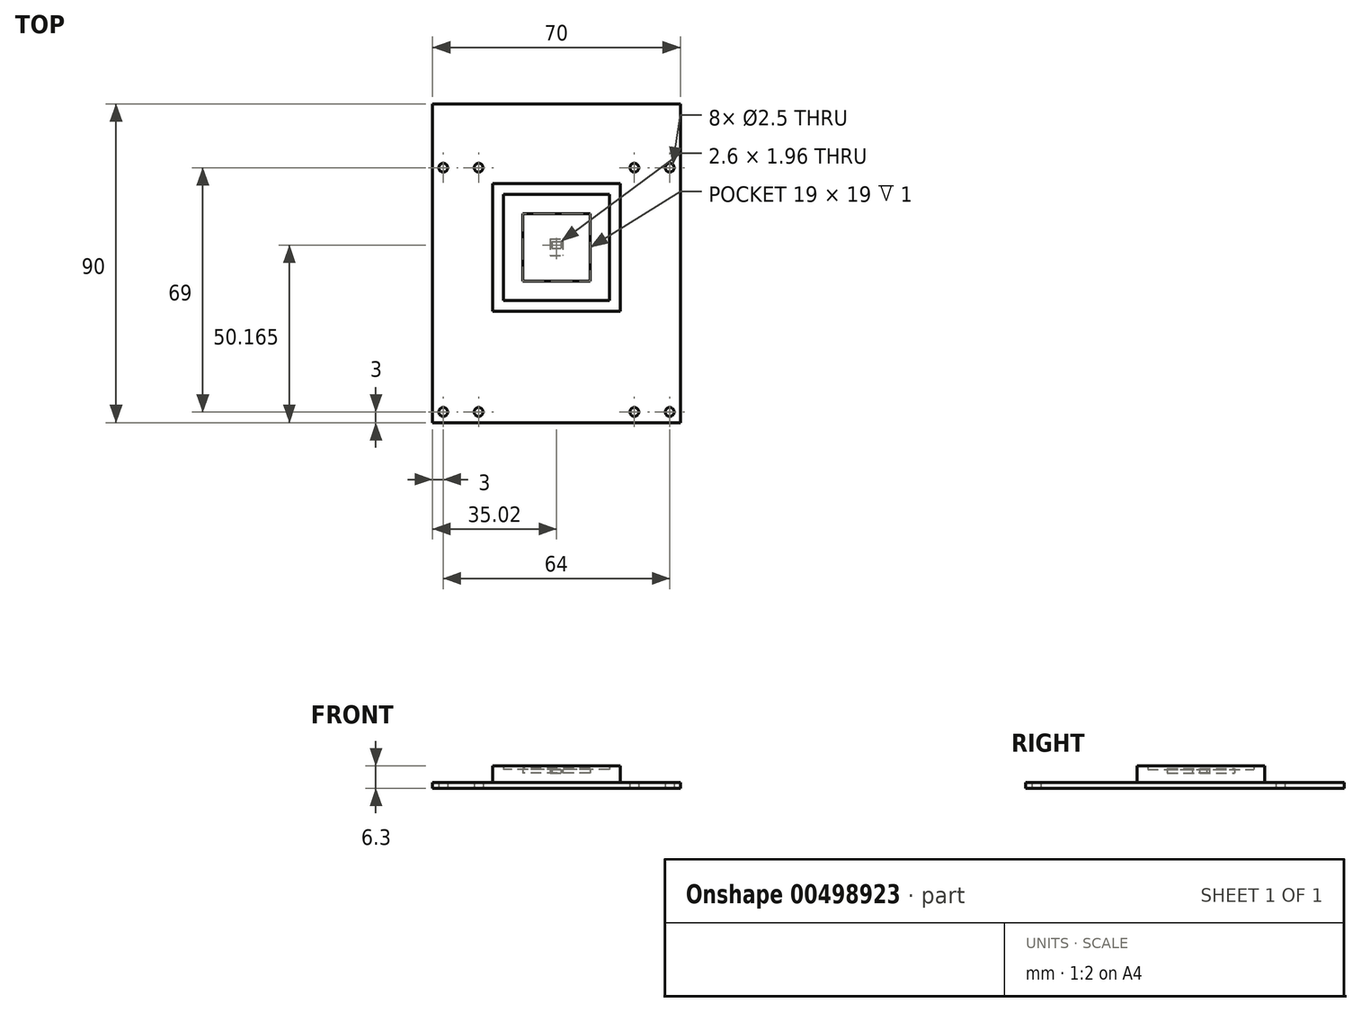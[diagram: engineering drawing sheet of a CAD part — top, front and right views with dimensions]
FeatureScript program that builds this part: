
annotation { "Feature Type Name" : "Feature", "Feature Type Description" : "" }
export const myFeature = defineFeature(function(context is Context, id is Id, definition is map)
    precondition{}
    {
        {
            var Q0;
            Q0=qCreatedBy(makeId("Top.planeOp"),FACE);
            var sketch = newSketch(context, id + "F0", { "sketchPlane" : qUnion([Q0])});
            skLineSegment(sketch, "E0.bottom", {"start": v(-1.83, 2.38) * mm, "end": v(1.83, 2.38) * mm, "construction": true});
            skLineSegment(sketch, "E0.top", {"start": v(-1.83, -2.37) * mm, "end": v(1.83, -2.37) * mm, "construction": true});
            skLineSegment(sketch, "E0.left", {"start": v(-1.83, 2.38) * mm, "end": v(-1.83, -2.37) * mm, "construction": true});
            skLineSegment(sketch, "E0.right", {"start": v(1.83, 2.38) * mm, "end": v(1.83, -2.37) * mm, "construction": true});
            skLineSegment(sketch, "E1.bottom", {"start": v(-1.28, 1.65) * mm, "end": v(1.32, 1.65) * mm, "construction": true});
            skLineSegment(sketch, "E1.top", {"start": v(-1.28, -0.31) * mm, "end": v(1.32, -0.31) * mm, "construction": true});
            skLineSegment(sketch, "E1.left", {"start": v(-1.28, 1.65) * mm, "end": v(-1.28, -0.31) * mm, "construction": true});
            skLineSegment(sketch, "E1.right", {"start": v(1.32, 1.65) * mm, "end": v(1.32, -0.31) * mm, "construction": true});
            skLineSegment(sketch, "E2", {"start": v(-1.28, 1.65) * mm, "end": v(1.32, -0.31) * mm, "construction": true});
            skLineSegment(sketch, "E3", {"start": v(1.32, 1.65) * mm, "end": v(-1.28, -0.31) * mm, "construction": true});
            skPoint(sketch, "E4", {"position": v(0.02, 0.67) * mm});
            skLineSegment(sketch, "E5.bottom", {"start": v(35, -49.5) * mm, "end": v(-35, -49.5) * mm, "construction": true});
            skLineSegment(sketch, "E5.top", {"start": v(35, 40.5) * mm, "end": v(-35, 40.5) * mm, "construction": true});
            skLineSegment(sketch, "E5.left", {"start": v(35, -49.5) * mm, "end": v(35, 40.5) * mm, "construction": true});
            skLineSegment(sketch, "E5.right", {"start": v(-35, -49.5) * mm, "end": v(-35, 40.5) * mm, "construction": true});
            skPoint(sketch, "E5.middle", {"position": v(0, 0) * mm});
            skLineSegment(sketch, "E6.bottom", {"start": v(18, -18) * mm, "end": v(-18, -18) * mm, "construction": true});
            skLineSegment(sketch, "E6.top", {"start": v(18, 18) * mm, "end": v(-18, 18) * mm, "construction": true});
            skLineSegment(sketch, "E6.left", {"start": v(18, -18) * mm, "end": v(18, 18) * mm, "construction": true});
            skLineSegment(sketch, "E6.right", {"start": v(-18, -18) * mm, "end": v(-18, 18) * mm, "construction": true});
            skPoint(sketch, "E7", {"position": v(-32, -46.5) * mm});
            skPoint(sketch, "E8", {"position": v(-22, -46.5) * mm});
            skPoint(sketch, "E9", {"position": v(22, -46.5) * mm});
            skPoint(sketch, "E10", {"position": v(32, -46.5) * mm});
            skPoint(sketch, "E11", {"position": v(32, 22.5) * mm});
            skPoint(sketch, "E12", {"position": v(22, 22.5) * mm});
            skPoint(sketch, "E12.positionSnap0", {"position": v(18, 0) * mm});
            skPoint(sketch, "E13", {"position": v(-22, 22.5) * mm});
            skPoint(sketch, "E14", {"position": v(-32, 22.5) * mm});
            skCircle(sketch, "E15", {"center": v(-32, 22.5) * mm, "radius": 1.25 * mm, "construction": true});
            skCircle(sketch, "E16", {"center": v(-22, 22.5) * mm, "radius": 1.25 * mm, "construction": true});
            skCircle(sketch, "E17", {"center": v(22, 22.5) * mm, "radius": 1.25 * mm, "construction": true});
            skCircle(sketch, "E18", {"center": v(32, 22.5) * mm, "radius": 1.25 * mm, "construction": true});
            skCircle(sketch, "E19", {"center": v(-32, -46.5) * mm, "radius": 1.25 * mm, "construction": true});
            skCircle(sketch, "E20", {"center": v(22, -46.5) * mm, "radius": 1.25 * mm, "construction": true});
            skCircle(sketch, "E21", {"center": v(32, -46.5) * mm, "radius": 1.25 * mm, "construction": true});
            skCircle(sketch, "E22", {"center": v(-22, -46.5) * mm, "radius": 1.25 * mm, "construction": true});
            skLineSegment(sketch, "E23.bottom", {"start": v(15, -15) * mm, "end": v(-15, -15) * mm, "construction": true});
            skLineSegment(sketch, "E23.top", {"start": v(15, 15) * mm, "end": v(-15, 15) * mm, "construction": true});
            skLineSegment(sketch, "E23.left", {"start": v(15, -15) * mm, "end": v(15, 15) * mm, "construction": true});
            skLineSegment(sketch, "E23.right", {"start": v(-15, -15) * mm, "end": v(-15, 15) * mm, "construction": true});
            skLineSegment(sketch, "E24.bottom", {"start": v(9.5, -9.5) * mm, "end": v(-9.5, -9.5) * mm, "construction": true});
            skLineSegment(sketch, "E24.top", {"start": v(9.5, 9.5) * mm, "end": v(-9.5, 9.5) * mm, "construction": true});
            skLineSegment(sketch, "E24.left", {"start": v(9.5, -9.5) * mm, "end": v(9.5, 9.5) * mm, "construction": true});
            skLineSegment(sketch, "E24.right", {"start": v(-9.5, -9.5) * mm, "end": v(-9.5, 9.5) * mm, "construction": true});
            skSolve(sketch);
        }
        {
            var Q0;
            Q0=qCreatedBy(makeId("Top.planeOp"),FACE);
            var sketch = newSketch(context, id + "F1", { "sketchPlane" : qUnion([Q0])});
            skLineSegment(sketch, "E25.0", {"start": v(-35, -49.5) * mm, "end": v(-35, 40.5) * mm});
            skLineSegment(sketch, "E26.0", {"start": v(35, 40.5) * mm, "end": v(-35, 40.5) * mm});
            skLineSegment(sketch, "E27.0", {"start": v(35, -49.5) * mm, "end": v(35, 40.5) * mm});
            skLineSegment(sketch, "E28.0", {"start": v(35, -49.5) * mm, "end": v(-35, -49.5) * mm});
            skCircle(sketch, "E29.0", {"center": v(-32, -46.5) * mm, "radius": 1.25 * mm});
            skPoint(sketch, "E30.0", {"position": v(32, -46.5) * mm});
            skCircle(sketch, "E31.0", {"center": v(22, -46.5) * mm, "radius": 1.25 * mm});
            skCircle(sketch, "E31.1", {"center": v(32, -46.5) * mm, "radius": 1.25 * mm});
            skCircle(sketch, "E32.0", {"center": v(-32, 22.5) * mm, "radius": 1.25 * mm});
            skCircle(sketch, "E32.1", {"center": v(-22, 22.5) * mm, "radius": 1.25 * mm});
            skCircle(sketch, "E33.0", {"center": v(22, 22.5) * mm, "radius": 1.25 * mm});
            skCircle(sketch, "E33.1", {"center": v(32, 22.5) * mm, "radius": 1.25 * mm});
            skCircle(sketch, "E34.0", {"center": v(-22, -46.5) * mm, "radius": 1.25 * mm});
            skSolve(sketch);
        }
        {
            var Q0;
            Q0=makeQuery(id+"F1.imprint","IMPRINT",FACE,{"disambiguationData":[TD([[makeQuery(id+"F1.imprint","IMPRINT",EDGE,{"derivedFrom":sQuery(id+"F1.wireOp",EDGE,"E25.0")}),-1.0]])]});
            extrude(context, id + "F2", {"entities" : qUnion([Q0]), "depth" : 1.65 * mm});
        }
        {
            var Q0;
            Q0=makeQuery(id+"F2.opExtrude","CAP_FACE",FACE,{"disambiguationData":[OSD([sQuery(id+"F1.wireOp",EDGE,"E25.0"),sQuery(id+"F1.wireOp",EDGE,"E26.0"),sQuery(id+"F1.wireOp",EDGE,"E27.0"),sQuery(id+"F1.wireOp",EDGE,"E28.0"),sQuery(id+"F1.wireOp",EDGE,"E31.0"),sQuery(id+"F1.wireOp",EDGE,"E31.1"),sQuery(id+"F1.wireOp",EDGE,"E32.0"),sQuery(id+"F1.wireOp",EDGE,"E32.1"),sQuery(id+"F1.wireOp",EDGE,"E33.0"),sQuery(id+"F1.wireOp",EDGE,"E33.1"),sQuery(id+"F1.wireOp",EDGE,"E34.0"),sQuery(id+"F1.wireOp",EDGE,"E29.0")])],"isStart":false});
            var sketch = newSketch(context, id + "F3", { "sketchPlane" : qUnion([Q0])});
            skLineSegment(sketch, "E35.0", {"start": v(18, 18) * mm, "end": v(-18, 18) * mm});
            skLineSegment(sketch, "E36.0", {"start": v(-18, -18) * mm, "end": v(-18, 18) * mm});
            skLineSegment(sketch, "E37.0", {"start": v(18, -18) * mm, "end": v(-18, -18) * mm});
            skLineSegment(sketch, "E38.0", {"start": v(18, -18) * mm, "end": v(18, 18) * mm});
            skLineSegment(sketch, "E39.0", {"start": v(15, 15) * mm, "end": v(-15, 15) * mm});
            skPoint(sketch, "E40.0", {"position": v(-15, 0) * mm});
            skLineSegment(sketch, "E41.0", {"start": v(-15, -15) * mm, "end": v(-15, 15) * mm});
            skLineSegment(sketch, "E42.0", {"start": v(15, -15) * mm, "end": v(-15, -15) * mm});
            skLineSegment(sketch, "E43.0", {"start": v(15, -15) * mm, "end": v(15, 15) * mm});
            skSolve(sketch);
        }
        {
            var Q0;
            Q0=makeQuery(id+"F3.imprint","IMPRINT",FACE,{"disambiguationData":[TD([[makeQuery(id+"F3.imprint","IMPRINT",EDGE,{"derivedFrom":sQuery(id+"F3.wireOp",EDGE,"E35.0")}),1.0]])]});
            extrude(context, id + "F4", {"entities" : qUnion([Q0]), "depth" : 4.65 * mm});
        }
        {
            var Q0;
            Q0=makeQuery(id+"F3.imprint","IMPRINT",FACE,{"disambiguationData":[TD([[makeQuery(id+"F3.imprint","IMPRINT",EDGE,{"derivedFrom":sQuery(id+"F3.wireOp",EDGE,"E39.0")}),1.0]])]});
            extrude(context, id + "F5", {"entities" : qUnion([Q0]), "operationType" : NewBodyOperationType.ADD, "depth" : 0.5 * mm});
        }
        {
            var Q0;
            Q0=makeQuery(id+"F5.opExtrude","CAP_FACE",FACE,{"disambiguationData":[OSD([sQuery(id+"F3.wireOp",EDGE,"E39.0"),sQuery(id+"F3.wireOp",EDGE,"E41.0"),sQuery(id+"F3.wireOp",EDGE,"E42.0"),sQuery(id+"F3.wireOp",EDGE,"E43.0")])],"isStart":false});
            var sketch = newSketch(context, id + "F6", { "sketchPlane" : qUnion([Q0])});
            skLineSegment(sketch, "E44.0.0", {"start": v(-15, -15) * mm, "end": v(15, -15) * mm});
            skLineSegment(sketch, "E44.0.1", {"start": v(15, -15) * mm, "end": v(15, 15) * mm});
            skLineSegment(sketch, "E44.0.2", {"start": v(15, 15) * mm, "end": v(-15, 15) * mm});
            skLineSegment(sketch, "E44.0.3", {"start": v(-15, 15) * mm, "end": v(-15, -15) * mm});
            skLineSegment(sketch, "E45.0", {"start": v(-9.5, -9.5) * mm, "end": v(-9.5, 9.5) * mm});
            skLineSegment(sketch, "E46.0", {"start": v(9.5, 9.5) * mm, "end": v(-9.5, 9.5) * mm});
            skLineSegment(sketch, "E47.0", {"start": v(9.5, -9.5) * mm, "end": v(9.5, 9.5) * mm});
            skLineSegment(sketch, "E48.0", {"start": v(9.5, -9.5) * mm, "end": v(-9.5, -9.5) * mm});
            skSolve(sketch);
        }
        {
            var Q0;
            Q0=makeQuery(id+"F6.imprint","IMPRINT",FACE,{"disambiguationData":[TD([[makeQuery(id+"F6.imprint","IMPRINT",EDGE,{"derivedFrom":sQuery(id+"F6.wireOp",EDGE,"E44.0.0")}),-1.0]])]});
            extrude(context, id + "F7", {"entities" : qUnion([Q0]), "depth" : (4.65 - 1 - 0.5) * mm});
        }
        {
            var Q0;
            Q0=makeQuery(id+"F6.imprint","IMPRINT",FACE,{"disambiguationData":[TD([[makeQuery(id+"F6.imprint","IMPRINT",EDGE,{"derivedFrom":sQuery(id+"F6.wireOp",EDGE,"E45.0")}),-1.0]])]});
            extrude(context, id + "F8", {"entities" : qUnion([Q0]), "operationType" : NewBodyOperationType.ADD, "depth" : (4.65 - 1 - 0.5 - 1) * mm});
        }
        {
            var Q0;
            Q0=makeQuery(id+"F8.opExtrude","CAP_FACE",FACE,{"disambiguationData":[OSD([sQuery(id+"F6.wireOp",EDGE,"E45.0"),sQuery(id+"F6.wireOp",EDGE,"E46.0"),sQuery(id+"F6.wireOp",EDGE,"E47.0"),sQuery(id+"F6.wireOp",EDGE,"E48.0")])],"isStart":false});
            var sketch = newSketch(context, id + "F9", { "sketchPlane" : qUnion([Q0])});
            skLineSegment(sketch, "E49.0", {"start": v(-1.83, 2.38) * mm, "end": v(-1.83, -2.37) * mm});
            skLineSegment(sketch, "E50.0", {"start": v(-1.83, 2.38) * mm, "end": v(1.83, 2.38) * mm});
            skLineSegment(sketch, "E51.0", {"start": v(1.83, 2.38) * mm, "end": v(1.83, -2.37) * mm});
            skLineSegment(sketch, "E52.0", {"start": v(-1.83, -2.37) * mm, "end": v(1.83, -2.37) * mm});
            skLineSegment(sketch, "E53.0", {"start": v(-1.28, 1.65) * mm, "end": v(-1.28, -0.31) * mm});
            skPoint(sketch, "E54.0", {"position": v(0.02, 1.65) * mm});
            skLineSegment(sketch, "E55.0", {"start": v(1.32, 1.65) * mm, "end": v(1.32, -0.31) * mm});
            skLineSegment(sketch, "E56.0", {"start": v(-1.28, -0.31) * mm, "end": v(1.32, -0.31) * mm});
            skLineSegment(sketch, "E57.0", {"start": v(-1.28, 1.65) * mm, "end": v(1.32, 1.65) * mm});
            skPoint(sketch, "E58.0", {"position": v(0.02, 0.67) * mm});
            skSolve(sketch);
        }
        {
            var Q0;
            Q0=makeQuery(id+"F9.imprint","IMPRINT",FACE,{"disambiguationData":[TD([[makeQuery(id+"F9.imprint","IMPRINT",EDGE,{"derivedFrom":sQuery(id+"F9.wireOp",EDGE,"E49.0")}),1.0]])]});
            extrude(context, id + "F10", {"entities" : qUnion([Q0]), "depth" : 1 * mm});
        }
        {
            var Q0;
            Q0=makeQuery(id+"F9.imprint","IMPRINT",FACE,{"disambiguationData":[TD([[makeQuery(id+"F9.imprint","IMPRINT",EDGE,{"derivedFrom":sQuery(id+"F9.wireOp",EDGE,"E53.0")}),1.0]])]});
            extrude(context, id + "F11", {"entities" : qUnion([Q0]), "depth" : 1 * mm});
        }
        {
            var Q0;
            Q0=makeQuery(id+"F9.imprint","IMPRINT",FACE,{"disambiguationData":[TD([[makeQuery(id+"F9.imprint","IMPRINT",EDGE,{"derivedFrom":sQuery(id+"F9.wireOp",EDGE,"E49.0")}),-1.0]])]});
            var sketch = newSketch(context, id + "F12", { "sketchPlane" : qUnion([Q0])});
            skLineSegment(sketch, "E59.0.0", {"start": v(-9.5, -9.5) * mm, "end": v(9.5, -9.5) * mm});
            skLineSegment(sketch, "E59.0.1", {"start": v(9.5, -9.5) * mm, "end": v(9.5, 9.5) * mm});
            skLineSegment(sketch, "E59.0.2", {"start": v(9.5, 9.5) * mm, "end": v(-9.5, 9.5) * mm});
            skLineSegment(sketch, "E59.0.3", {"start": v(-9.5, 9.5) * mm, "end": v(-9.5, -9.5) * mm});
            skSolve(sketch);
        }
        {
            var Q0;
            Q0=qSketchRegion(id+"F12",true);
            extrude(context, id + "F13", {"entities" : qUnion([Q0]), "depth" : 1.3 * mm});
        }
    });
